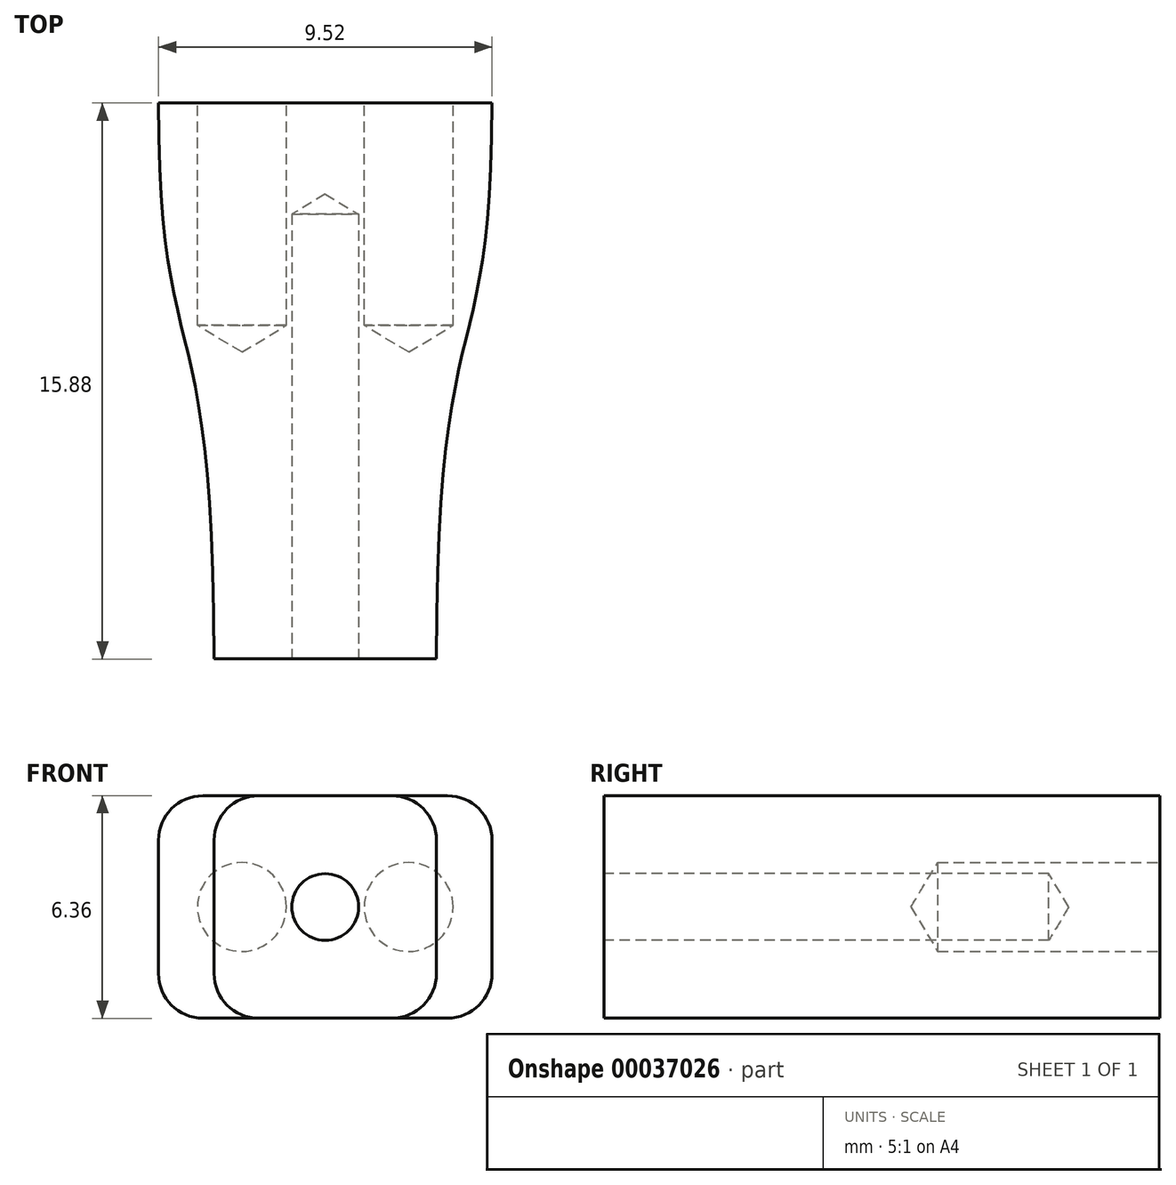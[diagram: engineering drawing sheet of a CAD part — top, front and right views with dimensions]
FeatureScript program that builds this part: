
annotation { "Feature Type Name" : "Feature", "Feature Type Description" : "" }
export const myFeature = defineFeature(function(context is Context, id is Id, definition is map)
    precondition{}
    {
        {
            var Q0;
            Q0=qCreatedBy(makeId("Front.planeOp"),FACE);
            var sketch = newSketch(context, id + "F0", { "sketchPlane" : qUnion([Q0])});
            skLineSegment(sketch, "E0.rect.bottom", {"start": v(4.76, 3.18) * mm, "end": v(-4.76, 3.18) * mm});
            skLineSegment(sketch, "E0.rect.top", {"start": v(4.76, -3.17) * mm, "end": v(-4.76, -3.17) * mm});
            skLineSegment(sketch, "E0.rect.left", {"start": v(4.76, 3.18) * mm, "end": v(4.76, -3.17) * mm});
            skLineSegment(sketch, "E0.rect.right", {"start": v(-4.76, 3.18) * mm, "end": v(-4.76, -3.17) * mm});
            skPoint(sketch, "E0.rect.middle", {"position": v(0, 0) * mm});
            skSolve(sketch);
        }
        {
            var Q0;
            Q0=qCreatedBy(makeId("Front.planeOp"),FACE);
            cPlane(context, id + "F1", {"entities" : qUnion([Q0]), "cplaneType" : CPlaneType.OFFSET, "offset" : 15.88 * mm, "width" : 152.4 * mm, "height" : 152.4 * mm});
        }
        {
            var Q0;
            Q0=qCreatedBy(id+"F1.planeOp",FACE);
            var sketch = newSketch(context, id + "F2", { "sketchPlane" : qUnion([Q0])});
            skLineSegment(sketch, "E1.rect.bottom", {"start": v(3.17, 3.18) * mm, "end": v(-3.18, 3.18) * mm});
            skLineSegment(sketch, "E1.rect.top", {"start": v(3.18, -3.17) * mm, "end": v(-3.18, -3.18) * mm});
            skLineSegment(sketch, "E1.rect.left", {"start": v(3.17, 3.18) * mm, "end": v(3.18, -3.18) * mm});
            skLineSegment(sketch, "E1.rect.right", {"start": v(-3.18, 3.17) * mm, "end": v(-3.18, -3.18) * mm});
            skPoint(sketch, "E1.rect.middle", {"position": v(0, 0) * mm});
            skSolve(sketch);
        }
        {
            var Q0;
            Q0=makeQuery(id+"F0.imprint","IMPRINT",FACE,{"disambiguationData":[TD([[makeQuery(id+"F0.imprint","IMPRINT",EDGE,{"derivedFrom":sQuery(id+"F0.wireOp",EDGE,"E0.rect.bottom")}),1.0]])]});
            var Q1;
            Q1=makeQuery(id+"F2.imprint","IMPRINT",FACE,{"disambiguationData":[TD([[makeQuery(id+"F2.imprint","IMPRINT",EDGE,{"derivedFrom":sQuery(id+"F2.wireOp",EDGE,"E1.rect.bottom")}),1.0]])]});
            loft(context, id + "F3", {"startCondition" : LoftEndDerivativeType.NORMAL_TO_PROFILE, "startMagnitude" : 1.5, "endCondition" : LoftEndDerivativeType.NORMAL_TO_PROFILE, "endMagnitude" : 2, "sheetProfilesArray" : [{ "sheetProfileEntities" : qUnion([Q0]) }, { "sheetProfileEntities" : qUnion([Q1]) }]});
        }
        {
            var Q0;
            Q0=makeQuery(id+"F3.opLoft","CAP_FACE",FACE,{"disambiguationData":[OSD([makeQuery(id+"F0.imprint","IMPRINT",FACE,{"disambiguationData":[TD([[makeQuery(id+"F0.imprint","IMPRINT",EDGE,{"derivedFrom":sQuery(id+"F0.wireOp",EDGE,"E0.rect.bottom")}),1.0]])]})])],"isStart":true});
            var sketch = newSketch(context, id + "F4", { "sketchPlane" : qUnion([Q0])});
            skLineSegment(sketch, "E2", {"start": v(-2.38, 0) * mm, "end": v(2.38, 0) * mm, "construction": true});
            skSolve(sketch);
        }
        {
            var Q0;
            Q0=makeQuery(id+"F3.opLoft","CAP_FACE",FACE,{"disambiguationData":[OSD([makeQuery(id+"F2.imprint","IMPRINT",FACE,{"disambiguationData":[TD([[makeQuery(id+"F2.imprint","IMPRINT",EDGE,{"derivedFrom":sQuery(id+"F2.wireOp",EDGE,"E1.rect.bottom")}),1.0]])]})])],"isStart":true});
            var sketch = newSketch(context, id + "F5", { "sketchPlane" : qUnion([Q0])});
            skPoint(sketch, "E3", {"position": v(0, 0) * mm});
            skSolve(sketch);
        }
        {
            var Q0;
            Q0=sQuery(id+"F4.wireOp",VERTEX,"E2.start");
            var Q1;
            Q1=sQuery(id+"F4.wireOp",VERTEX,"E2.end");
            var Q2;
            Q2=makeQuery(id+"F3.opLoft","SWEPT_BODY",BODY,{"disambiguationData":[OSD([makeQuery(id+"F0.imprint","IMPRINT",FACE,{"disambiguationData":[TD([[makeQuery(id+"F0.imprint","IMPRINT",EDGE,{"derivedFrom":sQuery(id+"F0.wireOp",EDGE,"E0.rect.bottom")}),1.0]])]}),makeQuery(id+"F2.imprint","IMPRINT",FACE,{"disambiguationData":[TD([[makeQuery(id+"F2.imprint","IMPRINT",EDGE,{"derivedFrom":sQuery(id+"F2.wireOp",EDGE,"E1.rect.bottom")}),1.0]])]})])]});
            hole(context, id + "F6", {"style" : HoleStyle.SIMPLE, "holeDiameter" : 2.54 * mm, "endStyle" : HoleEndStyle.BLIND, "holeDepth" : 6.35 * mm, "locations" : qUnion([Q0, Q1]), "scope" : qUnion([Q2])});
        }
        {
            var Q0;
            Q0=sQuery(id+"F5.wireOp",VERTEX,"E3");
            var Q1;
            Q1=makeQuery(id+"F3.opLoft","SWEPT_BODY",BODY,{"disambiguationData":[OSD([makeQuery(id+"F0.imprint","IMPRINT",FACE,{"disambiguationData":[TD([[makeQuery(id+"F0.imprint","IMPRINT",EDGE,{"derivedFrom":sQuery(id+"F0.wireOp",EDGE,"E0.rect.bottom")}),1.0]])]}),makeQuery(id+"F2.imprint","IMPRINT",FACE,{"disambiguationData":[TD([[makeQuery(id+"F2.imprint","IMPRINT",EDGE,{"derivedFrom":sQuery(id+"F2.wireOp",EDGE,"E1.rect.bottom")}),1.0]])]})])]});
            hole(context, id + "F7", {"style" : HoleStyle.SIMPLE, "holeDiameter" : 1.9 * mm, "endStyle" : HoleEndStyle.BLIND, "holeDepth" : 12.7 * mm, "locations" : qUnion([Q0]), "scope" : qUnion([Q1])});
        }
        {
            var Q0;
            Q0=makeQuery(id+"F3.opLoft","SWEPT_EDGE",EDGE,{"disambiguationData":[OSD([sQuery(id+"F0.wireOp",EDGE,"E0.rect.bottom"),sQuery(id+"F0.wireOp",EDGE,"E0.rect.left"),sQuery(id+"F2.wireOp",EDGE,"E1.rect.bottom"),sQuery(id+"F2.wireOp",EDGE,"E1.rect.left")])]});
            var Q1;
            Q1=makeQuery(id+"F3.opLoft","SWEPT_EDGE",EDGE,{"disambiguationData":[OSD([sQuery(id+"F0.wireOp",EDGE,"E0.rect.bottom"),sQuery(id+"F0.wireOp",EDGE,"E0.rect.right"),sQuery(id+"F2.wireOp",EDGE,"E1.rect.bottom"),sQuery(id+"F2.wireOp",EDGE,"E1.rect.right")])]});
            var Q2;
            Q2=makeQuery(id+"F3.opLoft","SWEPT_EDGE",EDGE,{"disambiguationData":[OSD([sQuery(id+"F0.wireOp",EDGE,"E0.rect.top"),sQuery(id+"F0.wireOp",EDGE,"E0.rect.left"),sQuery(id+"F2.wireOp",EDGE,"E1.rect.top"),sQuery(id+"F2.wireOp",EDGE,"E1.rect.left")])]});
            var Q3;
            Q3=makeQuery(id+"F3.opLoft","SWEPT_EDGE",EDGE,{"disambiguationData":[OSD([sQuery(id+"F0.wireOp",EDGE,"E0.rect.top"),sQuery(id+"F0.wireOp",EDGE,"E0.rect.right"),sQuery(id+"F2.wireOp",EDGE,"E1.rect.top"),sQuery(id+"F2.wireOp",EDGE,"E1.rect.right")])]});
            fillet(context, id + "F8", {"entities" : qUnion([Q0, Q1, Q2, Q3]), "radius" : 1.27 * mm, "tangentPropagation" : true, "allowEdgeOverflow" : false});
        }
    });
